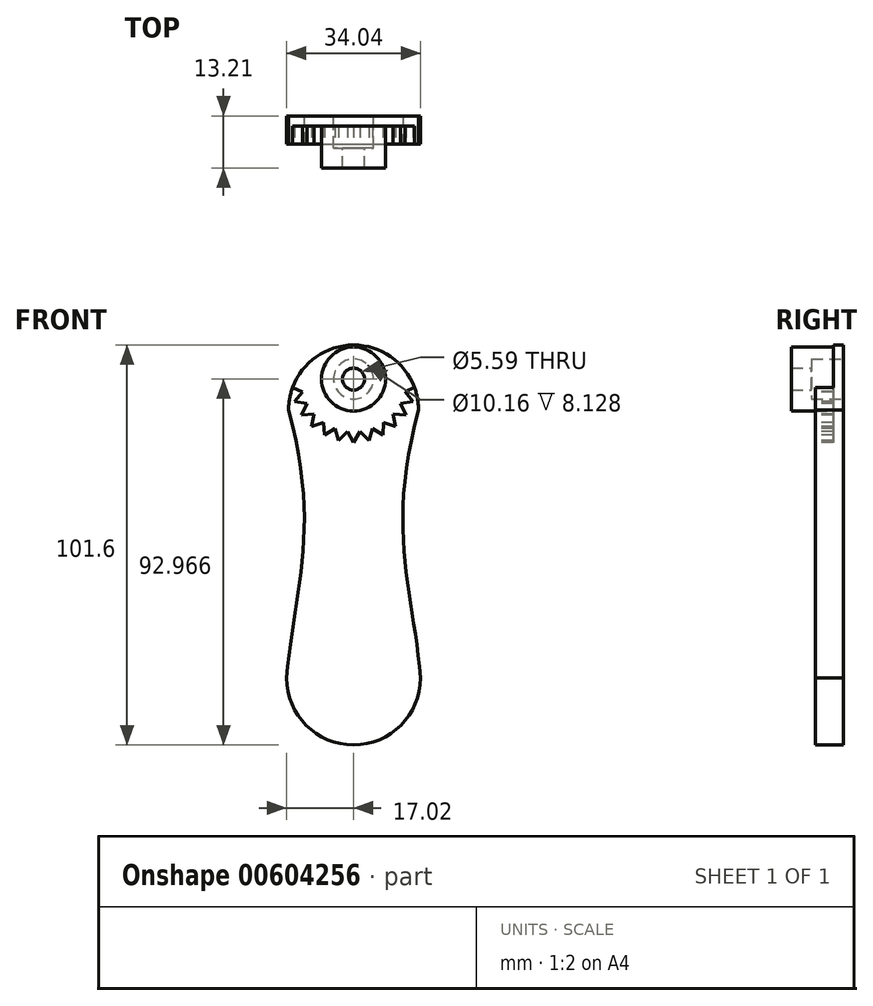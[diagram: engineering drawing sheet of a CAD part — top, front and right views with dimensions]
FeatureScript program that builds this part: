
annotation { "Feature Type Name" : "Feature", "Feature Type Description" : "" }
export const myFeature = defineFeature(function(context is Context, id is Id, definition is map)
    precondition{}
    {
        {
            var Q0;
            Q0=qCreatedBy(makeId("Front.planeOp"),FACE);
            var sketch = newSketch(context, id + "F0", { "sketchPlane" : qUnion([Q0])});
            skArc(sketch, "E0", {"start": v(16.51, 16.2) * mm, "mid": v(0, 32.71) * mm, "end": v(-16.51, 16.2) * mm});
            skArc(sketch, "E1", {"start": v(-17.02, -51.87) * mm, "mid": v(0, -68.89) * mm, "end": v(17.02, -51.87) * mm});
            skPoint(sketch, "E2", {"position": v(0, 32.71) * mm});
            skPoint(sketch, "E3", {"position": v(0, -68.89) * mm});
            skFitSpline(sketch, "E4", {"points": [v(-16.51, 16.2) * mm, v(-17.02, -51.87) * mm], "startDerivative": vector(24.94, -92.74) * mm, "endDerivative": vector(-5.66, -67.8) * mm});
            skFitSpline(sketch, "E5.MirrorCS", {"points": [v(16.51, 16.2) * mm, v(17.02, -51.87) * mm], "startDerivative": vector(-24.94, -92.74) * mm, "endDerivative": vector(5.66, -67.8) * mm});
            skLineSegment(sketch, "E6", {"start": v(-12.7, -17.82) * mm, "end": v(12.7, -17.82) * mm, "construction": true});
            skSolve(sketch);
        }
        {
            var Q0;
            Q0=makeQuery(id+"F0.imprint","IMPRINT",FACE,{"disambiguationData":[TD([[makeQuery(id+"F0.imprint","IMPRINT",EDGE,{"derivedFrom":sQuery(id+"F0.wireOp",EDGE,"E0")}),1.0]])]});
            extrude(context, id + "F1", {"entities" : qUnion([Q0]), "depth" : 7.11 * mm, "offsetDistance" : 25.4 * mm});
        }
        {
            var Q0;
            Q0=makeQuery(id+"F1.opExtrude","CAP_FACE",FACE,{"disambiguationData":[OSD([sQuery(id+"F0.wireOp",EDGE,"E0"),sQuery(id+"F0.wireOp",EDGE,"E1"),sQuery(id+"F0.wireOp",EDGE,"E4"),sQuery(id+"F0.wireOp",EDGE,"E5.MirrorCS")])],"isStart":false});
            var sketch = newSketch(context, id + "F2", { "sketchPlane" : qUnion([Q0])});
            skLineSegment(sketch, "E7", {"start": v(0, 32.71) * mm, "end": v(0, 24.08) * mm, "construction": true});
            skCircle(sketch, "E8", {"center": v(0, 24.08) * mm, "radius": 2.8 * mm});
            skCircle(sketch, "E9", {"center": v(0, 24.08) * mm, "radius": 8.13 * mm});
            skSolve(sketch);
        }
        {
            var Q0;
            Q0=makeQuery(id+"F2.imprint","IMPRINT",FACE,{"disambiguationData":[TD([[makeQuery(id+"F2.imprint","IMPRINT",EDGE,{"derivedFrom":sQuery(id+"F2.wireOp",EDGE,"E8")}),-1.0]])]});
            extrude(context, id + "F3", {"entities" : qUnion([Q0]), "operationType" : NewBodyOperationType.ADD, "depth" : 6.1 * mm, "offsetDistance" : 25.4 * mm});
        }
        {
            var Q0;
            Q0=makeQuery(id+"F3.boolean.opBoolean","SPLIT",FACE,{"disambiguationData":[TD([makeQuery(id+"F3.opExtrude","SWEPT_FACE",FACE,{"disambiguationData":[OSD([sQuery(id+"F2.wireOp",EDGE,"E8")])]})])],"derivedFrom":makeQuery(id+"F1.opExtrude","CAP_FACE",FACE,{"disambiguationData":[OSD([sQuery(id+"F0.wireOp",EDGE,"E0"),sQuery(id+"F0.wireOp",EDGE,"E1"),sQuery(id+"F0.wireOp",EDGE,"E4"),sQuery(id+"F0.wireOp",EDGE,"E5.MirrorCS")])],"isStart":false})});
            extrude(context, id + "F4", {"entities" : qUnion([Q0]), "operationType" : NewBodyOperationType.REMOVE, "endBound" : BoundingType.SYMMETRIC, "oppositeDirection" : true, "depth" : 101.6 * mm, "offsetDistance" : 25.4 * mm});
        }
        {
            var Q0;
            {var subQ0=sQuery(id+"F0.wireOp",EDGE,"E4");var subQ1=sQuery(id+"F0.wireOp",EDGE,"E1");var subQ2=sQuery(id+"F0.wireOp",EDGE,"E5.MirrorCS");var subQ3=sQuery(id+"F0.wireOp",EDGE,"E0");Q0=makeQuery(id+"F3.boolean.opBoolean","SPLIT",FACE,{"disambiguationData":[TD([makeQuery(id+"F1.opExtrude","SWEPT_FACE",FACE,{"disambiguationData":[OSD([subQ3])]})])],"derivedFrom":makeQuery(id+"F1.opExtrude","CAP_FACE",FACE,{"disambiguationData":[OSD([subQ3,subQ1,subQ0,subQ2])],"isStart":false})});}
            var sketch = newSketch(context, id + "F5", { "sketchPlane" : qUnion([Q0])});
            skLineSegment(sketch, "E10", {"start": v(0, 24.08) * mm, "end": v(0, 0) * mm, "construction": true});
            skLineSegment(sketch, "E11", {"start": v(-15.97, 22.08) * mm, "end": v(-12.93, 20.8) * mm});
            skLineSegment(sketch, "E12.1.0", {"start": v(-12.95, 20.88) * mm, "end": v(-15.03, 18.32) * mm});
            skLineSegment(sketch, "E12.1.1", {"start": v(-15.03, 18.32) * mm, "end": v(-11.77, 17.8) * mm});
            skLineSegment(sketch, "E12.2.0", {"start": v(-11.8, 17.88) * mm, "end": v(-13.21, 14.9) * mm});
            skLineSegment(sketch, "E12.2.1", {"start": v(-13.21, 14.9) * mm, "end": v(-9.92, 15.17) * mm});
            skLineSegment(sketch, "E12.3.0", {"start": v(-9.98, 15.23) * mm, "end": v(-10.63, 12) * mm});
            skLineSegment(sketch, "E12.3.1", {"start": v(-10.63, 12) * mm, "end": v(-7.5, 13.05) * mm});
            skLineSegment(sketch, "E12.4.0", {"start": v(-7.58, 13.1) * mm, "end": v(-7.43, 9.8) * mm});
            skLineSegment(sketch, "E12.4.1", {"start": v(-7.43, 9.8) * mm, "end": v(-4.65, 11.58) * mm});
            skLineSegment(sketch, "E12.5.0", {"start": v(-4.73, 11.6) * mm, "end": v(-3.8, 8.44) * mm});
            skLineSegment(sketch, "E12.5.1", {"start": v(-3.8, 8.44) * mm, "end": v(-1.52, 10.83) * mm});
            skLineSegment(sketch, "E12.6.0", {"start": v(-1.6, 10.84) * mm, "end": v(0.05, 7.98) * mm});
            skLineSegment(sketch, "E12.6.1", {"start": v(0.05, 7.98) * mm, "end": v(1.7, 10.85) * mm});
            skLineSegment(sketch, "E12.7.0", {"start": v(1.6, 10.84) * mm, "end": v(3.9, 8.46) * mm});
            skLineSegment(sketch, "E12.7.1", {"start": v(3.9, 8.46) * mm, "end": v(4.81, 11.64) * mm});
            skLineSegment(sketch, "E12.8.0", {"start": v(4.73, 11.6) * mm, "end": v(7.53, 9.85) * mm});
            skLineSegment(sketch, "E12.8.1", {"start": v(7.53, 9.85) * mm, "end": v(7.65, 13.15) * mm});
            skLineSegment(sketch, "E12.9.0", {"start": v(7.58, 13.1) * mm, "end": v(10.71, 12.07) * mm});
            skLineSegment(sketch, "E12.9.1", {"start": v(10.71, 12.07) * mm, "end": v(10.04, 15.3) * mm});
            skLineSegment(sketch, "E12.10.0", {"start": v(9.98, 15.23) * mm, "end": v(13.27, 14.98) * mm});
            skLineSegment(sketch, "E12.10.1", {"start": v(13.27, 14.98) * mm, "end": v(11.85, 17.96) * mm});
            skLineSegment(sketch, "E12.11.0", {"start": v(11.8, 17.88) * mm, "end": v(15.07, 18.42) * mm});
            skLineSegment(sketch, "E12.11.1", {"start": v(15.07, 18.42) * mm, "end": v(12.97, 20.97) * mm});
            skLineSegment(sketch, "E12.12.0", {"start": v(12.95, 20.88) * mm, "end": v(15.98, 22.19) * mm});
            skPoint(sketch, "E12.center", {"position": v(0, 24.08) * mm});
            skArc(sketch, "E13.trimOffspring", {"start": v(-13.33, 24.08) * mm, "mid": v(-13.33, 24.03) * mm, "end": v(-13.33, 23.99) * mm});
            skArc(sketch, "E14.trimOffspring", {"start": v(-12.95, 20.88) * mm, "mid": v(-12.94, 20.84) * mm, "end": v(-12.93, 20.8) * mm});
            skArc(sketch, "E15.trimOffspring", {"start": v(-11.8, 17.88) * mm, "mid": v(-11.79, 17.84) * mm, "end": v(-11.77, 17.8) * mm});
            skArc(sketch, "E16.trimOffspring", {"start": v(-9.98, 15.23) * mm, "mid": v(-9.95, 15.2) * mm, "end": v(-9.92, 15.17) * mm});
            skArc(sketch, "E17.trimOffspring", {"start": v(-7.58, 13.1) * mm, "mid": v(-7.54, 13.08) * mm, "end": v(-7.5, 13.05) * mm});
            skArc(sketch, "E18.trimOffspring", {"start": v(-4.73, 11.6) * mm, "mid": v(-4.69, 11.6) * mm, "end": v(-4.65, 11.58) * mm});
            skArc(sketch, "E19.trimOffspring", {"start": v(-1.6, 10.84) * mm, "mid": v(-1.56, 10.83) * mm, "end": v(-1.52, 10.83) * mm});
            skArc(sketch, "E20.trimOffspring", {"start": v(1.6, 10.84) * mm, "mid": v(1.65, 10.84) * mm, "end": v(1.7, 10.85) * mm});
            skArc(sketch, "E21.trimOffspring", {"start": v(4.73, 11.6) * mm, "mid": v(4.77, 11.62) * mm, "end": v(4.81, 11.64) * mm});
            skArc(sketch, "E22.trimOffspring", {"start": v(7.58, 13.1) * mm, "mid": v(7.61, 13.13) * mm, "end": v(7.65, 13.15) * mm});
            skArc(sketch, "E23.trimOffspring", {"start": v(11.8, 17.88) * mm, "mid": v(11.83, 17.92) * mm, "end": v(11.85, 17.96) * mm});
            skArc(sketch, "E24.trimOffspring", {"start": v(13.33, 24.08) * mm, "mid": v(13.33, 24.12) * mm, "end": v(13.33, 24.16) * mm});
            skArc(sketch, "E25.trimOffspring", {"start": v(12.95, 20.88) * mm, "mid": v(12.96, 20.93) * mm, "end": v(12.97, 20.97) * mm});
            skSolve(sketch);
        }
        {
            var Q0;
            Q0 = qSketchRegion(id + "F5", true);
            var Q1;
            {var subQ49=sQuery(id+"F5.wireOp",EDGE,"E14.trimOffspring");Q1=makeQuery(id+"F5.imprint","IMPRINT",FACE,{"disambiguationData":[TD([[makeQuery(id+"F5.imprint","IMPRINT",EDGE,{"derivedFrom":subQ49}),1.0]])]});}
            extrude(context, id + "F6", {"entities" : qUnion([Q0, Q1]), "operationType" : NewBodyOperationType.REMOVE, "oppositeDirection" : true, "depth" : 4.57 * mm, "offsetDistance" : 25.4 * mm});
        }
        {
            var Q0;
            Q0=makeQuery(id+"F1.opExtrude","CAP_FACE",FACE,{"disambiguationData":[OSD([sQuery(id+"F0.wireOp",EDGE,"E0"),sQuery(id+"F0.wireOp",EDGE,"E1"),sQuery(id+"F0.wireOp",EDGE,"E4"),sQuery(id+"F0.wireOp",EDGE,"E5.MirrorCS")])],"isStart":true});
            var sketch = newSketch(context, id + "F7", { "sketchPlane" : qUnion([Q0])});
            skLineSegment(sketch, "E26", {"start": v(0, 32.71) * mm, "end": v(0, 24.08) * mm, "construction": true});
            skCircle(sketch, "E27", {"center": v(0, 24.08) * mm, "radius": 5.08 * mm});
            skSolve(sketch);
        }
        {
            var Q0;
            Q0=makeQuery(id+"F7.imprint","IMPRINT",FACE,{"disambiguationData":[TD([[makeQuery(id+"F7.imprint","IMPRINT",EDGE,{"derivedFrom":sQuery(id+"F7.wireOp",EDGE,"E27")}),1.0]])]});
            extrude(context, id + "F8", {"entities" : qUnion([Q0]), "operationType" : NewBodyOperationType.REMOVE, "oppositeDirection" : true, "depth" : 8.13 * mm, "offsetDistance" : 25.4 * mm});
        }
    });
